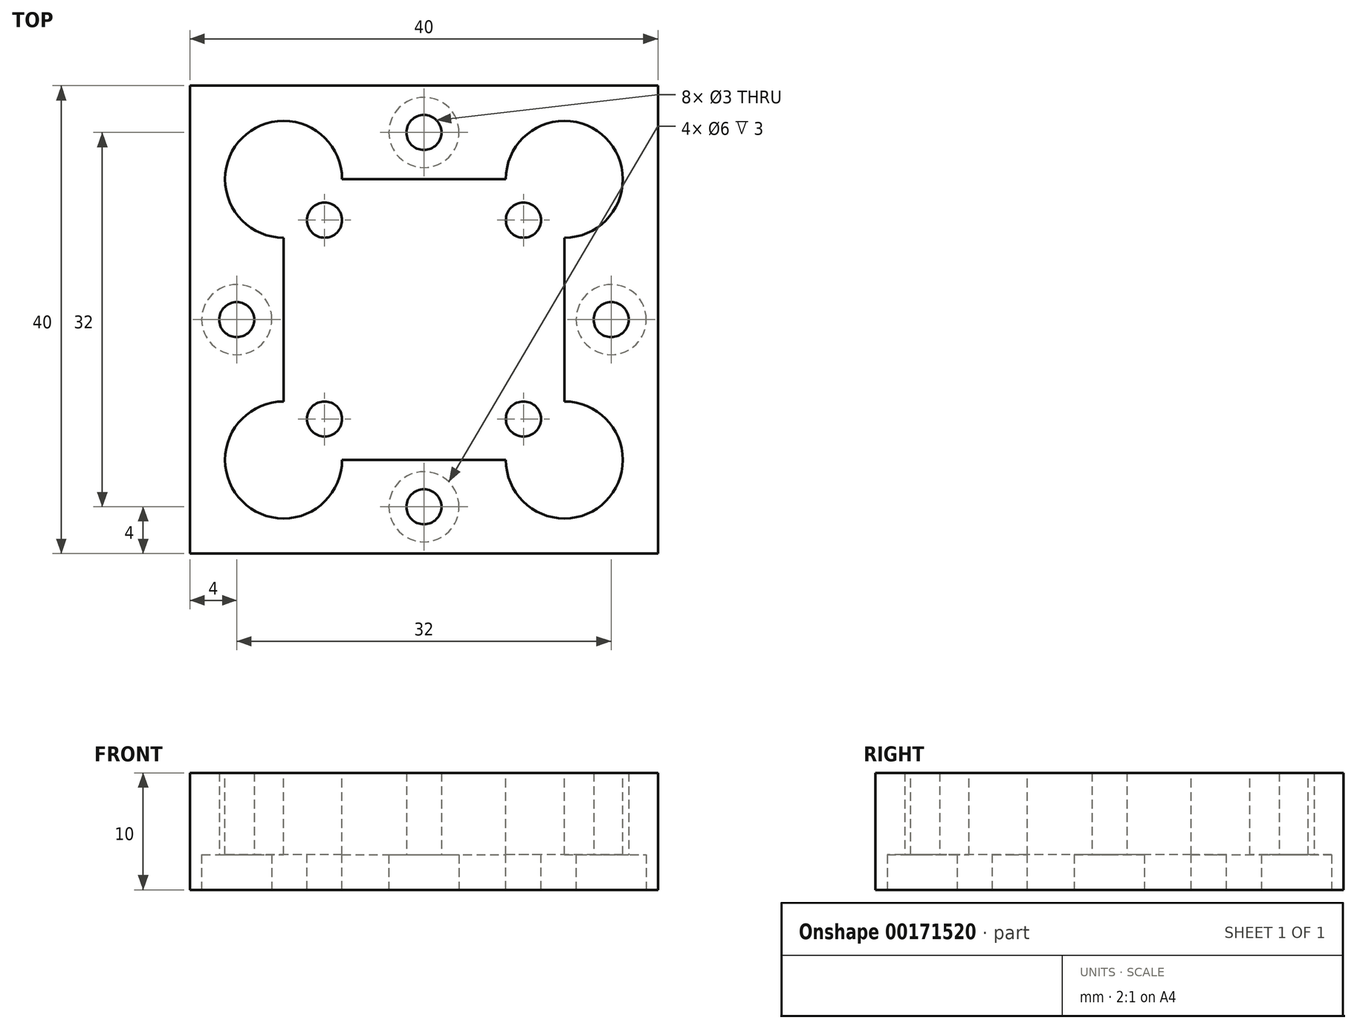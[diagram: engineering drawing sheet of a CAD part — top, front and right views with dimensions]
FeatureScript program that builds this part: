
annotation { "Feature Type Name" : "Feature", "Feature Type Description" : "" }
export const myFeature = defineFeature(function(context is Context, id is Id, definition is map)
    precondition{}
    {
        {
            var Q0;
            Q0=qCreatedBy(makeId("Top.planeOp"),FACE);
            var sketch = newSketch(context, id + "F0", { "sketchPlane" : qUnion([Q0])});
            skLineSegment(sketch, "E0.bottom", {"start": v(-20, 20) * mm, "end": v(20, 20) * mm});
            skLineSegment(sketch, "E0.top", {"start": v(-20, -20) * mm, "end": v(20, -20) * mm});
            skLineSegment(sketch, "E0.left", {"start": v(-20, 20) * mm, "end": v(-20, -20) * mm});
            skLineSegment(sketch, "E0.right", {"start": v(20, 20) * mm, "end": v(20, -20) * mm});
            skCircle(sketch, "E1", {"center": v(-16, 0) * mm, "radius": 1.5 * mm});
            skCircle(sketch, "E2", {"center": v(16, 0) * mm, "radius": 1.5 * mm});
            skCircle(sketch, "E3", {"center": v(0, 16) * mm, "radius": 1.5 * mm});
            skCircle(sketch, "E4", {"center": v(0, -16) * mm, "radius": 1.5 * mm});
            skPoint(sketch, "E5", {"position": v(-20, 0) * mm});
            skSolve(sketch);
        }
        {
            var Q0;
            Q0 = qSketchRegion(id + "F0", true);
            extrude(context, id + "F1", {"entities" : qUnion([Q0]), "depth" : 10 * mm});
        }
        {
            var Q0;
            Q0=makeQuery(id+"F1.opExtrude","CAP_FACE",FACE,{"disambiguationData":[OSD([sQuery(id+"F0.wireOp",EDGE,"E0.bottom"),sQuery(id+"F0.wireOp",EDGE,"E0.top"),sQuery(id+"F0.wireOp",EDGE,"E0.left"),sQuery(id+"F0.wireOp",EDGE,"E0.right")])],"isStart":false});
            var sketch = newSketch(context, id + "F2", { "sketchPlane" : qUnion([Q0])});
            skLineSegment(sketch, "E6.bottom", {"start": v(-7, 12) * mm, "end": v(7, 12) * mm});
            skLineSegment(sketch, "E6.top", {"start": v(-7, -12) * mm, "end": v(7, -12) * mm});
            skLineSegment(sketch, "E6.left", {"start": v(-12, 7) * mm, "end": v(-12, -7) * mm});
            skLineSegment(sketch, "E6.right", {"start": v(12, 7) * mm, "end": v(12, -7) * mm});
            skArc(sketch, "E7", {"start": v(-7, 12) * mm, "mid": v(-15.54, 15.54) * mm, "end": v(-12, 7) * mm});
            skArc(sketch, "E8", {"start": v(12, 7) * mm, "mid": v(15.54, 15.54) * mm, "end": v(7, 12) * mm});
            skArc(sketch, "E9", {"start": v(7, -12) * mm, "mid": v(15.54, -15.54) * mm, "end": v(12, -7) * mm});
            skArc(sketch, "E10", {"start": v(-12, -7) * mm, "mid": v(-15.54, -15.54) * mm, "end": v(-7, -12) * mm});
            skSolve(sketch);
        }
        {
            var Q0;
            Q0 = qSketchRegion(id + "F2", true);
            extrude(context, id + "F3", {"entities" : qUnion([Q0]), "operationType" : NewBodyOperationType.REMOVE, "oppositeDirection" : true, "depth" : 7 * mm});
        }
        {
            var Q0;
            Q0=makeQuery(id+"F1.opExtrude","CAP_FACE",FACE,{"disambiguationData":[OSD([sQuery(id+"F0.wireOp",EDGE,"E0.bottom"),sQuery(id+"F0.wireOp",EDGE,"E0.top"),sQuery(id+"F0.wireOp",EDGE,"E0.left"),sQuery(id+"F0.wireOp",EDGE,"E0.right"),sQuery(id+"F0.wireOp",EDGE,"E1"),sQuery(id+"F0.wireOp",EDGE,"E2"),sQuery(id+"F0.wireOp",EDGE,"E3"),sQuery(id+"F0.wireOp",EDGE,"E4")])],"isStart":true});
            var sketch = newSketch(context, id + "F4", { "sketchPlane" : qUnion([Q0])});
            skCircle(sketch, "E11", {"center": v(0, 16) * mm, "radius": 3 * mm});
            skCircle(sketch, "E12", {"center": v(-16, 0) * mm, "radius": 3 * mm});
            skCircle(sketch, "E13", {"center": v(0, -16) * mm, "radius": 3 * mm});
            skCircle(sketch, "E14", {"center": v(16, 0) * mm, "radius": 3 * mm});
            skSolve(sketch);
        }
        {
            var Q0;
            Q0 = qSketchRegion(id + "F4", true);
            extrude(context, id + "F5", {"entities" : qUnion([Q0]), "operationType" : NewBodyOperationType.REMOVE, "oppositeDirection" : true, "depth" : 3 * mm});
        }
        {
            var Q0;
            Q0=makeQuery(id+"F3.boolean.opBoolean","COPY",FACE,{"derivedFrom":makeQuery(id+"F3.opExtrude","CAP_FACE",FACE,{"disambiguationData":[OSD([sQuery(id+"F2.wireOp",EDGE,"E6.bottom"),sQuery(id+"F2.wireOp",EDGE,"E6.top"),sQuery(id+"F2.wireOp",EDGE,"E6.left"),sQuery(id+"F2.wireOp",EDGE,"E6.right"),sQuery(id+"F2.wireOp",EDGE,"E7"),sQuery(id+"F2.wireOp",EDGE,"E8"),sQuery(id+"F2.wireOp",EDGE,"E9"),sQuery(id+"F2.wireOp",EDGE,"E10")])],"isStart":false})});
            var sketch = newSketch(context, id + "F6", { "sketchPlane" : qUnion([Q0])});
            skCircle(sketch, "E15", {"center": v(-8.5, 8.5) * mm, "radius": 1.5 * mm});
            skCircle(sketch, "E16", {"center": v(8.5, 8.5) * mm, "radius": 1.5 * mm});
            skCircle(sketch, "E17", {"center": v(-8.5, -8.5) * mm, "radius": 1.5 * mm});
            skCircle(sketch, "E18", {"center": v(8.5, -8.5) * mm, "radius": 1.5 * mm});
            skSolve(sketch);
        }
        {
            var Q0;
            Q0 = qSketchRegion(id + "F6", true);
            extrude(context, id + "F7", {"entities" : qUnion([Q0]), "operationType" : NewBodyOperationType.REMOVE, "endBound" : BoundingType.THROUGH_ALL, "oppositeDirection" : true, "depth" : 25 * mm});
        }
    });
